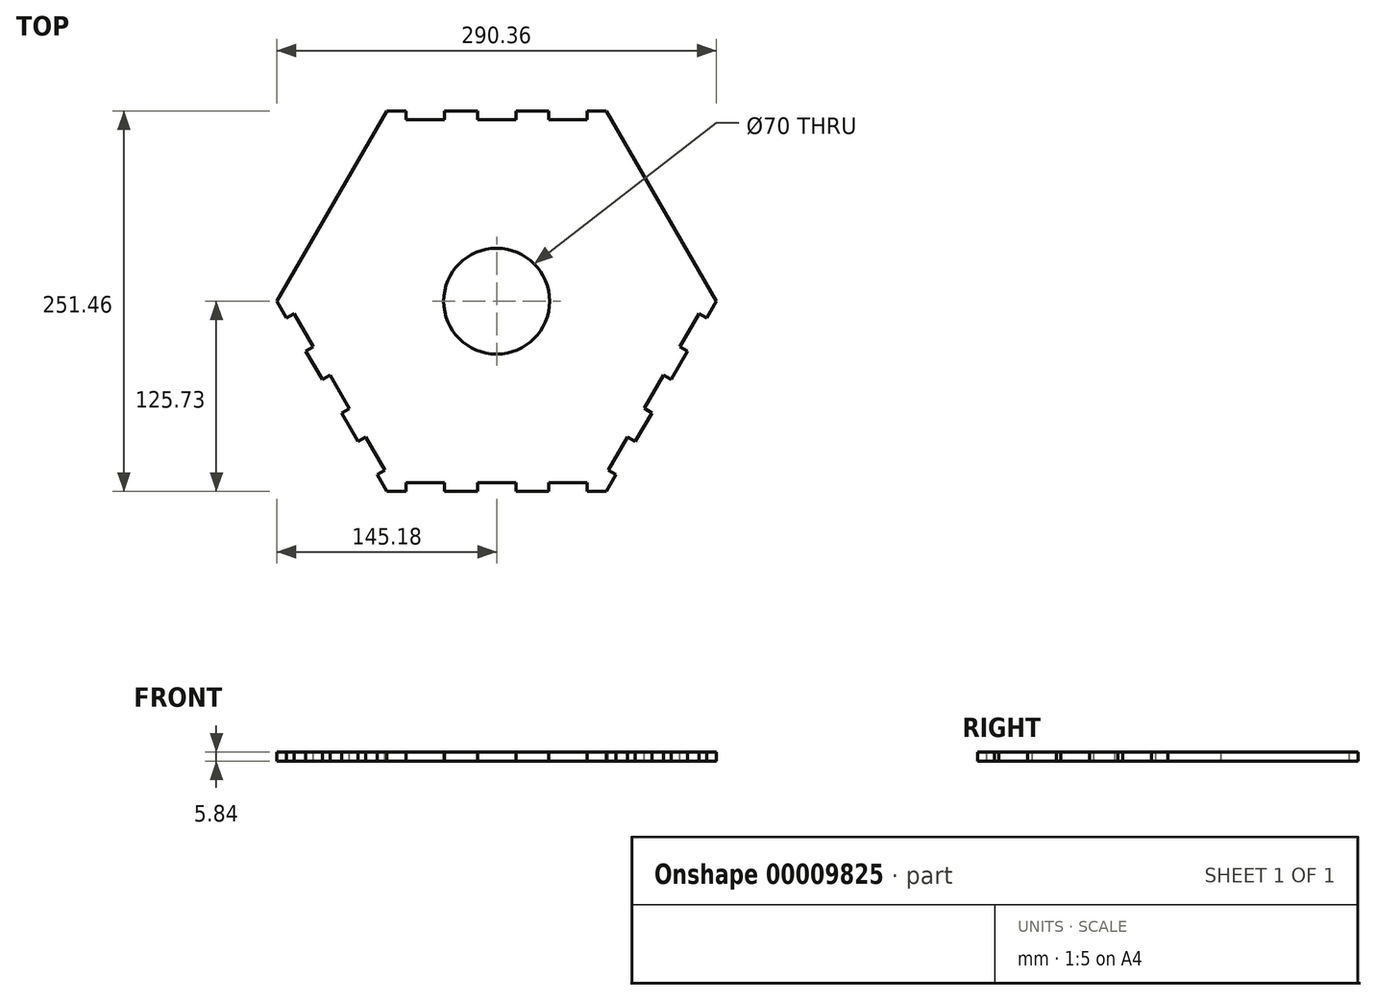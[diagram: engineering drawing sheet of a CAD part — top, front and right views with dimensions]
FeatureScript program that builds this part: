
annotation { "Feature Type Name" : "Feature", "Feature Type Description" : "" }
export const myFeature = defineFeature(function(context is Context, id is Id, definition is map)
    precondition{}
    {
        {
            var Q0;
            Q0=qCreatedBy(makeId("Top.planeOp"),FACE);
            var sketch = newSketch(context, id + "F0", { "sketchPlane" : qUnion([Q0])});
            skCircle(sketch, "E0.cCircle", {"center": v(0, 0) * mm, "radius": 125.73 * mm, "construction": true});
            skLineSegment(sketch, "E0.0", {"start": v(-72.6, 125.73) * mm, "end": v(72.6, 125.73) * mm});
            skLineSegment(sketch, "E0.1", {"start": v(72.6, 125.73) * mm, "end": v(145.18, 0) * mm});
            skLineSegment(sketch, "E0.2", {"start": v(145.18, 0) * mm, "end": v(72.6, -125.73) * mm});
            skLineSegment(sketch, "E0.3", {"start": v(72.6, -125.73) * mm, "end": v(-72.6, -125.73) * mm});
            skLineSegment(sketch, "E0.4", {"start": v(-72.6, -125.73) * mm, "end": v(-145.18, 0) * mm});
            skLineSegment(sketch, "E0.5", {"start": v(-145.18, 0) * mm, "end": v(-72.6, 125.73) * mm});
            skPoint(sketch, "E0.0.midPoint", {"position": v(0, 125.73) * mm});
            skSolve(sketch);
        }
        {
            var Q0;
            Q0=makeQuery(id+"F0.imprint","IMPRINT",FACE,{"disambiguationData":[TD([[makeQuery(id+"F0.imprint","IMPRINT",EDGE,{"derivedFrom":sQuery(id+"F0.wireOp",EDGE,"E0.0")}),-1.0]])]});
            var Q1;
            Q1=makeQuery(id+"F0.imprint","IMPRINT",FACE,{"disambiguationData":[TD([[makeQuery(id+"F0.imprint","IMPRINT",EDGE,{"derivedFrom":sQuery(id+"F0.wireOp",EDGE,"7ca5dedf-ea6b-4b1c-8738-69444ab6b368.0")}),-1.0]])]});
            extrude(context, id + "F1", {"entities" : qUnion([Q0, Q1]), "depth" : 5.84 * mm});
        }
        {
            var Q0;
            Q0=makeQuery(id+"F1.opExtrude","CAP_FACE",FACE,{"disambiguationData":[OSD([sQuery(id+"F0.wireOp",EDGE,"E0.0"),sQuery(id+"F0.wireOp",EDGE,"E0.1"),sQuery(id+"F0.wireOp",EDGE,"E0.2"),sQuery(id+"F0.wireOp",EDGE,"E0.3"),sQuery(id+"F0.wireOp",EDGE,"E0.4"),sQuery(id+"F0.wireOp",EDGE,"E0.5")])],"isStart":false});
            var sketch = newSketch(context, id + "F2", { "sketchPlane" : qUnion([Q0])});
            skLineSegment(sketch, "E1.bottom", {"start": v(-59.9, -125.73) * mm, "end": v(-34.5, -125.73) * mm});
            skLineSegment(sketch, "E1.top", {"start": v(-59.9, -119.89) * mm, "end": v(-34.5, -119.89) * mm});
            skLineSegment(sketch, "E1.left", {"start": v(-59.9, -125.73) * mm, "end": v(-59.9, -119.89) * mm});
            skLineSegment(sketch, "E1.right", {"start": v(-34.5, -125.73) * mm, "end": v(-34.5, -119.89) * mm});
            skLineSegment(sketch, "E2.bottom", {"start": v(34.5, -125.73) * mm, "end": v(59.9, -125.73) * mm});
            skLineSegment(sketch, "E2.top", {"start": v(34.5, -119.89) * mm, "end": v(59.9, -119.89) * mm});
            skLineSegment(sketch, "E2.left", {"start": v(34.5, -125.73) * mm, "end": v(34.5, -119.89) * mm});
            skLineSegment(sketch, "E2.right", {"start": v(59.9, -125.73) * mm, "end": v(59.9, -119.89) * mm});
            skLineSegment(sketch, "E3.bottom", {"start": v(-12.7, -125.73) * mm, "end": v(12.7, -125.73) * mm});
            skLineSegment(sketch, "E3.top", {"start": v(-12.7, -119.89) * mm, "end": v(12.7, -119.89) * mm});
            skLineSegment(sketch, "E3.left", {"start": v(-12.7, -125.73) * mm, "end": v(-12.7, -119.89) * mm});
            skLineSegment(sketch, "E3.right", {"start": v(12.7, -125.73) * mm, "end": v(12.7, -119.89) * mm});
            skPoint(sketch, "E4", {"position": v(0, -119.89) * mm});
            skLineSegment(sketch, "E5.1.0", {"start": v(138.83, 11) * mm, "end": v(133.77, 8.08) * mm});
            skLineSegment(sketch, "E5.1.1", {"start": v(133.77, 8.08) * mm, "end": v(121.07, 30.07) * mm});
            skLineSegment(sketch, "E5.1.2", {"start": v(138.83, 11) * mm, "end": v(126.13, 33) * mm});
            skLineSegment(sketch, "E5.1.3", {"start": v(126.13, 33) * mm, "end": v(121.07, 30.07) * mm});
            skLineSegment(sketch, "E5.1.4", {"start": v(115.23, 51.87) * mm, "end": v(110.17, 48.95) * mm});
            skLineSegment(sketch, "E5.1.5", {"start": v(110.17, 48.95) * mm, "end": v(97.47, 70.95) * mm});
            skLineSegment(sketch, "E5.1.6", {"start": v(115.23, 51.87) * mm, "end": v(102.53, 73.87) * mm});
            skLineSegment(sketch, "E5.1.7", {"start": v(102.53, 73.87) * mm, "end": v(97.47, 70.95) * mm});
            skLineSegment(sketch, "E5.1.8", {"start": v(86.58, 89.81) * mm, "end": v(73.88, 111.81) * mm});
            skLineSegment(sketch, "E5.1.9", {"start": v(91.64, 92.73) * mm, "end": v(78.94, 114.73) * mm});
            skLineSegment(sketch, "E5.1.10", {"start": v(91.64, 92.73) * mm, "end": v(86.58, 89.81) * mm});
            skLineSegment(sketch, "E5.1.11", {"start": v(78.94, 114.73) * mm, "end": v(73.88, 111.81) * mm});
            skLineSegment(sketch, "E5.2.0", {"start": v(-78.94, 114.73) * mm, "end": v(-73.88, 111.81) * mm});
            skLineSegment(sketch, "E5.2.1", {"start": v(-73.88, 111.81) * mm, "end": v(-86.58, 89.81) * mm});
            skLineSegment(sketch, "E5.2.2", {"start": v(-78.94, 114.73) * mm, "end": v(-91.64, 92.73) * mm});
            skLineSegment(sketch, "E5.2.3", {"start": v(-91.64, 92.73) * mm, "end": v(-86.58, 89.81) * mm});
            skLineSegment(sketch, "E5.2.4", {"start": v(-102.54, 73.86) * mm, "end": v(-97.48, 70.94) * mm});
            skLineSegment(sketch, "E5.2.5", {"start": v(-97.48, 70.94) * mm, "end": v(-110.18, 48.94) * mm});
            skLineSegment(sketch, "E5.2.6", {"start": v(-102.54, 73.86) * mm, "end": v(-115.24, 51.86) * mm});
            skLineSegment(sketch, "E5.2.7", {"start": v(-115.24, 51.86) * mm, "end": v(-110.18, 48.94) * mm});
            skLineSegment(sketch, "E5.2.8", {"start": v(-121.07, 30.07) * mm, "end": v(-133.77, 8.08) * mm});
            skLineSegment(sketch, "E5.2.9", {"start": v(-126.13, 33) * mm, "end": v(-138.83, 11) * mm});
            skLineSegment(sketch, "E5.2.10", {"start": v(-126.13, 33) * mm, "end": v(-121.07, 30.07) * mm});
            skLineSegment(sketch, "E5.2.11", {"start": v(-138.83, 11) * mm, "end": v(-133.77, 8.08) * mm});
            skPoint(sketch, "E5.center", {"position": v(0, 0) * mm});
            skLineSegment(sketch, "E6.1.0", {"start": v(78.94, -114.73) * mm, "end": v(73.88, -111.81) * mm});
            skLineSegment(sketch, "E6.1.1", {"start": v(73.88, -111.81) * mm, "end": v(86.58, -89.81) * mm});
            skLineSegment(sketch, "E6.1.2", {"start": v(78.94, -114.73) * mm, "end": v(91.64, -92.73) * mm});
            skLineSegment(sketch, "E6.1.3", {"start": v(91.64, -92.73) * mm, "end": v(86.58, -89.81) * mm});
            skLineSegment(sketch, "E6.1.4", {"start": v(102.54, -73.86) * mm, "end": v(97.48, -70.94) * mm});
            skLineSegment(sketch, "E6.1.5", {"start": v(97.48, -70.94) * mm, "end": v(110.18, -48.94) * mm});
            skLineSegment(sketch, "E6.1.6", {"start": v(102.54, -73.86) * mm, "end": v(115.24, -51.86) * mm});
            skLineSegment(sketch, "E6.1.7", {"start": v(115.24, -51.86) * mm, "end": v(110.18, -48.94) * mm});
            skLineSegment(sketch, "E6.1.8", {"start": v(126.13, -33) * mm, "end": v(121.07, -30.07) * mm});
            skLineSegment(sketch, "E6.1.9", {"start": v(121.07, -30.07) * mm, "end": v(133.77, -8.08) * mm});
            skLineSegment(sketch, "E6.1.10", {"start": v(126.13, -33) * mm, "end": v(138.83, -11) * mm});
            skLineSegment(sketch, "E6.1.11", {"start": v(138.83, -11) * mm, "end": v(133.77, -8.08) * mm});
            skLineSegment(sketch, "E6.3.0", {"start": v(59.9, 125.73) * mm, "end": v(59.9, 119.89) * mm});
            skLineSegment(sketch, "E6.3.1", {"start": v(59.9, 119.89) * mm, "end": v(34.5, 119.89) * mm});
            skLineSegment(sketch, "E6.3.2", {"start": v(59.9, 125.73) * mm, "end": v(34.5, 125.73) * mm});
            skLineSegment(sketch, "E6.3.3", {"start": v(34.5, 125.73) * mm, "end": v(34.5, 119.89) * mm});
            skLineSegment(sketch, "E6.3.4", {"start": v(12.7, 125.73) * mm, "end": v(12.7, 119.89) * mm});
            skLineSegment(sketch, "E6.3.5", {"start": v(12.7, 119.89) * mm, "end": v(-12.7, 119.89) * mm});
            skLineSegment(sketch, "E6.3.6", {"start": v(12.7, 125.73) * mm, "end": v(-12.7, 125.73) * mm});
            skLineSegment(sketch, "E6.3.7", {"start": v(-12.7, 125.73) * mm, "end": v(-12.7, 119.89) * mm});
            skLineSegment(sketch, "E6.3.8", {"start": v(-34.5, 125.73) * mm, "end": v(-34.5, 119.89) * mm});
            skLineSegment(sketch, "E6.3.9", {"start": v(-34.5, 119.89) * mm, "end": v(-59.9, 119.89) * mm});
            skLineSegment(sketch, "E6.3.10", {"start": v(-34.5, 125.73) * mm, "end": v(-59.9, 125.73) * mm});
            skLineSegment(sketch, "E6.3.11", {"start": v(-59.9, 125.73) * mm, "end": v(-59.9, 119.89) * mm});
            skLineSegment(sketch, "E6.5.0", {"start": v(-138.83, -11) * mm, "end": v(-133.77, -8.08) * mm});
            skLineSegment(sketch, "E6.5.1", {"start": v(-133.77, -8.08) * mm, "end": v(-121.07, -30.07) * mm});
            skLineSegment(sketch, "E6.5.2", {"start": v(-138.83, -11) * mm, "end": v(-126.13, -33) * mm});
            skLineSegment(sketch, "E6.5.3", {"start": v(-126.13, -33) * mm, "end": v(-121.07, -30.07) * mm});
            skLineSegment(sketch, "E6.5.4", {"start": v(-115.23, -51.87) * mm, "end": v(-110.17, -48.95) * mm});
            skLineSegment(sketch, "E6.5.5", {"start": v(-110.17, -48.95) * mm, "end": v(-97.47, -70.95) * mm});
            skLineSegment(sketch, "E6.5.6", {"start": v(-115.23, -51.87) * mm, "end": v(-102.53, -73.87) * mm});
            skLineSegment(sketch, "E6.5.7", {"start": v(-102.53, -73.87) * mm, "end": v(-97.47, -70.95) * mm});
            skLineSegment(sketch, "E6.5.8", {"start": v(-91.64, -92.73) * mm, "end": v(-86.58, -89.81) * mm});
            skLineSegment(sketch, "E6.5.9", {"start": v(-86.58, -89.81) * mm, "end": v(-73.88, -111.81) * mm});
            skLineSegment(sketch, "E6.5.10", {"start": v(-91.64, -92.73) * mm, "end": v(-78.94, -114.73) * mm});
            skLineSegment(sketch, "E6.5.11", {"start": v(-78.94, -114.73) * mm, "end": v(-73.88, -111.81) * mm});
            skSolve(sketch);
        }
        {
            var Q0;
            Q0=makeQuery(id+"F2.imprint","IMPRINT",FACE,{"disambiguationData":[TD([[makeQuery(id+"F2.imprint","IMPRINT",EDGE,{"derivedFrom":sQuery(id+"F2.wireOp",EDGE,"E1.bottom")}),-1.0]])]});
            var Q1;
            Q1=makeQuery(id+"F2.imprint","IMPRINT",FACE,{"disambiguationData":[TD([[makeQuery(id+"F2.imprint","IMPRINT",EDGE,{"derivedFrom":sQuery(id+"F2.wireOp",EDGE,"E3.bottom")}),-1.0]])]});
            var Q2;
            Q2=makeQuery(id+"F2.imprint","IMPRINT",FACE,{"disambiguationData":[TD([[makeQuery(id+"F2.imprint","IMPRINT",EDGE,{"derivedFrom":sQuery(id+"F2.wireOp",EDGE,"E2.bottom")}),-1.0]])]});
            var Q3;
            Q3=makeQuery(id+"F2.imprint","IMPRINT",FACE,{"disambiguationData":[TD([[makeQuery(id+"F2.imprint","IMPRINT",EDGE,{"derivedFrom":sQuery(id+"F2.wireOp",EDGE,"E6.5.8")}),-1.0]])]});
            var Q4;
            Q4=makeQuery(id+"F2.imprint","IMPRINT",FACE,{"disambiguationData":[TD([[makeQuery(id+"F2.imprint","IMPRINT",EDGE,{"derivedFrom":sQuery(id+"F2.wireOp",EDGE,"E6.5.4")}),-1.0]])]});
            var Q5;
            Q5=makeQuery(id+"F2.imprint","IMPRINT",FACE,{"disambiguationData":[TD([[makeQuery(id+"F2.imprint","IMPRINT",EDGE,{"derivedFrom":sQuery(id+"F2.wireOp",EDGE,"E6.5.0")}),-1.0]])]});
            var Q6;
            Q6=makeQuery(id+"F2.imprint","IMPRINT",FACE,{"disambiguationData":[TD([[makeQuery(id+"F2.imprint","IMPRINT",EDGE,{"derivedFrom":sQuery(id+"F2.wireOp",EDGE,"E5.2.10")}),-1.0]])]});
            var Q7;
            Q7=makeQuery(id+"F2.imprint","IMPRINT",FACE,{"disambiguationData":[TD([[makeQuery(id+"F2.imprint","IMPRINT",EDGE,{"derivedFrom":sQuery(id+"F2.wireOp",EDGE,"E5.2.4")}),-1.0]])]});
            var Q8;
            Q8=makeQuery(id+"F2.imprint","IMPRINT",FACE,{"disambiguationData":[TD([[makeQuery(id+"F2.imprint","IMPRINT",EDGE,{"derivedFrom":sQuery(id+"F2.wireOp",EDGE,"E5.2.0")}),-1.0]])]});
            var Q9;
            Q9=makeQuery(id+"F2.imprint","IMPRINT",FACE,{"disambiguationData":[TD([[makeQuery(id+"F2.imprint","IMPRINT",EDGE,{"derivedFrom":sQuery(id+"F2.wireOp",EDGE,"E6.3.8")}),-1.0]])]});
            var Q10;
            Q10=makeQuery(id+"F2.imprint","IMPRINT",FACE,{"disambiguationData":[TD([[makeQuery(id+"F2.imprint","IMPRINT",EDGE,{"derivedFrom":sQuery(id+"F2.wireOp",EDGE,"E6.3.4")}),-1.0]])]});
            var Q11;
            Q11=makeQuery(id+"F2.imprint","IMPRINT",FACE,{"disambiguationData":[TD([[makeQuery(id+"F2.imprint","IMPRINT",EDGE,{"derivedFrom":sQuery(id+"F2.wireOp",EDGE,"E6.3.0")}),-1.0]])]});
            var Q12;
            Q12=makeQuery(id+"F2.imprint","IMPRINT",FACE,{"disambiguationData":[TD([[makeQuery(id+"F2.imprint","IMPRINT",EDGE,{"derivedFrom":sQuery(id+"F2.wireOp",EDGE,"E5.1.10")}),-1.0]])]});
            var Q13;
            Q13=makeQuery(id+"F2.imprint","IMPRINT",FACE,{"disambiguationData":[TD([[makeQuery(id+"F2.imprint","IMPRINT",EDGE,{"derivedFrom":sQuery(id+"F2.wireOp",EDGE,"E5.1.4")}),-1.0]])]});
            var Q14;
            Q14=makeQuery(id+"F2.imprint","IMPRINT",FACE,{"disambiguationData":[TD([[makeQuery(id+"F2.imprint","IMPRINT",EDGE,{"derivedFrom":sQuery(id+"F2.wireOp",EDGE,"E5.1.0")}),-1.0]])]});
            var Q15;
            Q15=makeQuery(id+"F2.imprint","IMPRINT",FACE,{"disambiguationData":[TD([[makeQuery(id+"F2.imprint","IMPRINT",EDGE,{"derivedFrom":sQuery(id+"F2.wireOp",EDGE,"E6.1.8")}),-1.0]])]});
            var Q16;
            Q16=makeQuery(id+"F2.imprint","IMPRINT",FACE,{"disambiguationData":[TD([[makeQuery(id+"F2.imprint","IMPRINT",EDGE,{"derivedFrom":sQuery(id+"F2.wireOp",EDGE,"E6.1.4")}),-1.0]])]});
            var Q17;
            Q17=makeQuery(id+"F2.imprint","IMPRINT",FACE,{"disambiguationData":[TD([[makeQuery(id+"F2.imprint","IMPRINT",EDGE,{"derivedFrom":sQuery(id+"F2.wireOp",EDGE,"E6.1.0")}),-1.0]])]});
            var Q18;
            Q18=makeQuery(id+"F1.opExtrude","CAP_FACE",FACE,{"disambiguationData":[OSD([sQuery(id+"F0.wireOp",EDGE,"E0.0"),sQuery(id+"F0.wireOp",EDGE,"E0.1"),sQuery(id+"F0.wireOp",EDGE,"E0.2"),sQuery(id+"F0.wireOp",EDGE,"E0.3"),sQuery(id+"F0.wireOp",EDGE,"E0.4"),sQuery(id+"F0.wireOp",EDGE,"E0.5")])],"isStart":true});
            extrude(context, id + "F3", {"entities" : qUnion([Q0, Q1, Q2, Q3, Q4, Q5, Q6, Q7, Q8, Q9, Q10, Q11, Q12, Q13, Q14, Q15, Q16, Q17]), "operationType" : NewBodyOperationType.REMOVE, "endBound" : BoundingType.UP_TO_SURFACE, "oppositeDirection" : true, "endBoundEntityFace" : qUnion([Q18]), "depth" : 25.4 * mm});
        }
        {
            var Q0;
            Q0=makeQuery(id+"F1.opExtrude","CAP_FACE",FACE,{"disambiguationData":[OSD([sQuery(id+"F0.wireOp",EDGE,"E0.0"),sQuery(id+"F0.wireOp",EDGE,"E0.1"),sQuery(id+"F0.wireOp",EDGE,"E0.2"),sQuery(id+"F0.wireOp",EDGE,"E0.3"),sQuery(id+"F0.wireOp",EDGE,"E0.4"),sQuery(id+"F0.wireOp",EDGE,"E0.5")])],"isStart":false});
            var sketch = newSketch(context, id + "F4", { "sketchPlane" : qUnion([Q0])});
            skCircle(sketch, "E7", {"center": v(0, 0) * mm, "radius": 35 * mm});
            skSolve(sketch);
        }
        {
            var Q0;
            Q0=makeQuery(id+"F4.imprint","IMPRINT",FACE,{"disambiguationData":[TD([[makeQuery(id+"F4.imprint","IMPRINT",EDGE,{"derivedFrom":sQuery(id+"F4.wireOp",EDGE,"E7")}),1.0]])]});
            var Q1;
            Q1=makeQuery(id+"F1.opExtrude","CAP_FACE",FACE,{"disambiguationData":[OSD([sQuery(id+"F0.wireOp",EDGE,"E0.0"),sQuery(id+"F0.wireOp",EDGE,"E0.1"),sQuery(id+"F0.wireOp",EDGE,"E0.2"),sQuery(id+"F0.wireOp",EDGE,"E0.3"),sQuery(id+"F0.wireOp",EDGE,"E0.4"),sQuery(id+"F0.wireOp",EDGE,"E0.5")])],"isStart":true});
            extrude(context, id + "F5", {"entities" : qUnion([Q0]), "operationType" : NewBodyOperationType.REMOVE, "endBound" : BoundingType.UP_TO_SURFACE, "oppositeDirection" : true, "endBoundEntityFace" : qUnion([Q1]), "depth" : 25.4 * mm});
        }
    });
